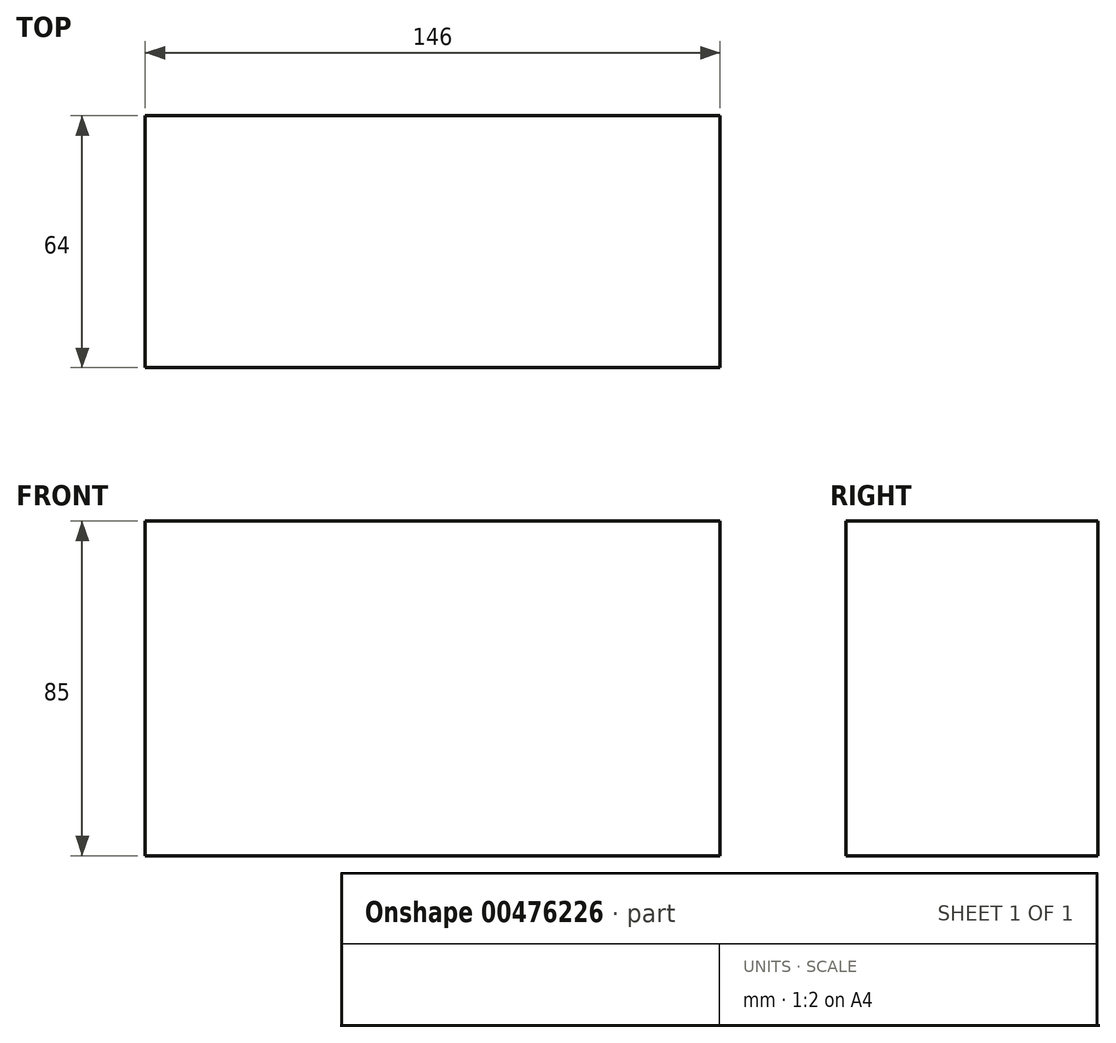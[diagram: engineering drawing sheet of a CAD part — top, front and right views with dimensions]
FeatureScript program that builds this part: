
annotation { "Feature Type Name" : "Feature", "Feature Type Description" : "" }
export const myFeature = defineFeature(function(context is Context, id is Id, definition is map)
    precondition{}
    {
        {
            var Q0;
            Q0=qCreatedBy(makeId("Top.planeOp"),FACE);
            var sketch = newSketch(context, id + "F0", { "sketchPlane" : qUnion([Q0])});
            skLineSegment(sketch, "E0.bottom", {"start": v(-80.88, 18.76) * mm, "end": v(65.12, 18.76) * mm});
            skLineSegment(sketch, "E0.top", {"start": v(-80.88, -45.24) * mm, "end": v(65.12, -45.24) * mm});
            skLineSegment(sketch, "E0.left", {"start": v(-80.88, 18.76) * mm, "end": v(-80.88, -45.24) * mm});
            skLineSegment(sketch, "E0.right", {"start": v(65.12, 18.76) * mm, "end": v(65.12, -45.24) * mm});
            skSolve(sketch);
        }
        {
            var Q0;
            Q0=makeQuery(id+"F0.imprint","IMPRINT",FACE,{"disambiguationData":[TD([[makeQuery(id+"F0.imprint","IMPRINT",EDGE,{"derivedFrom":sQuery(id+"F0.wireOp",EDGE,"E0.bottom")}),-1.0]])]});
            extrude(context, id + "F1", {"entities" : qUnion([Q0]), "depth" : 85 * mm});
        }
    });
